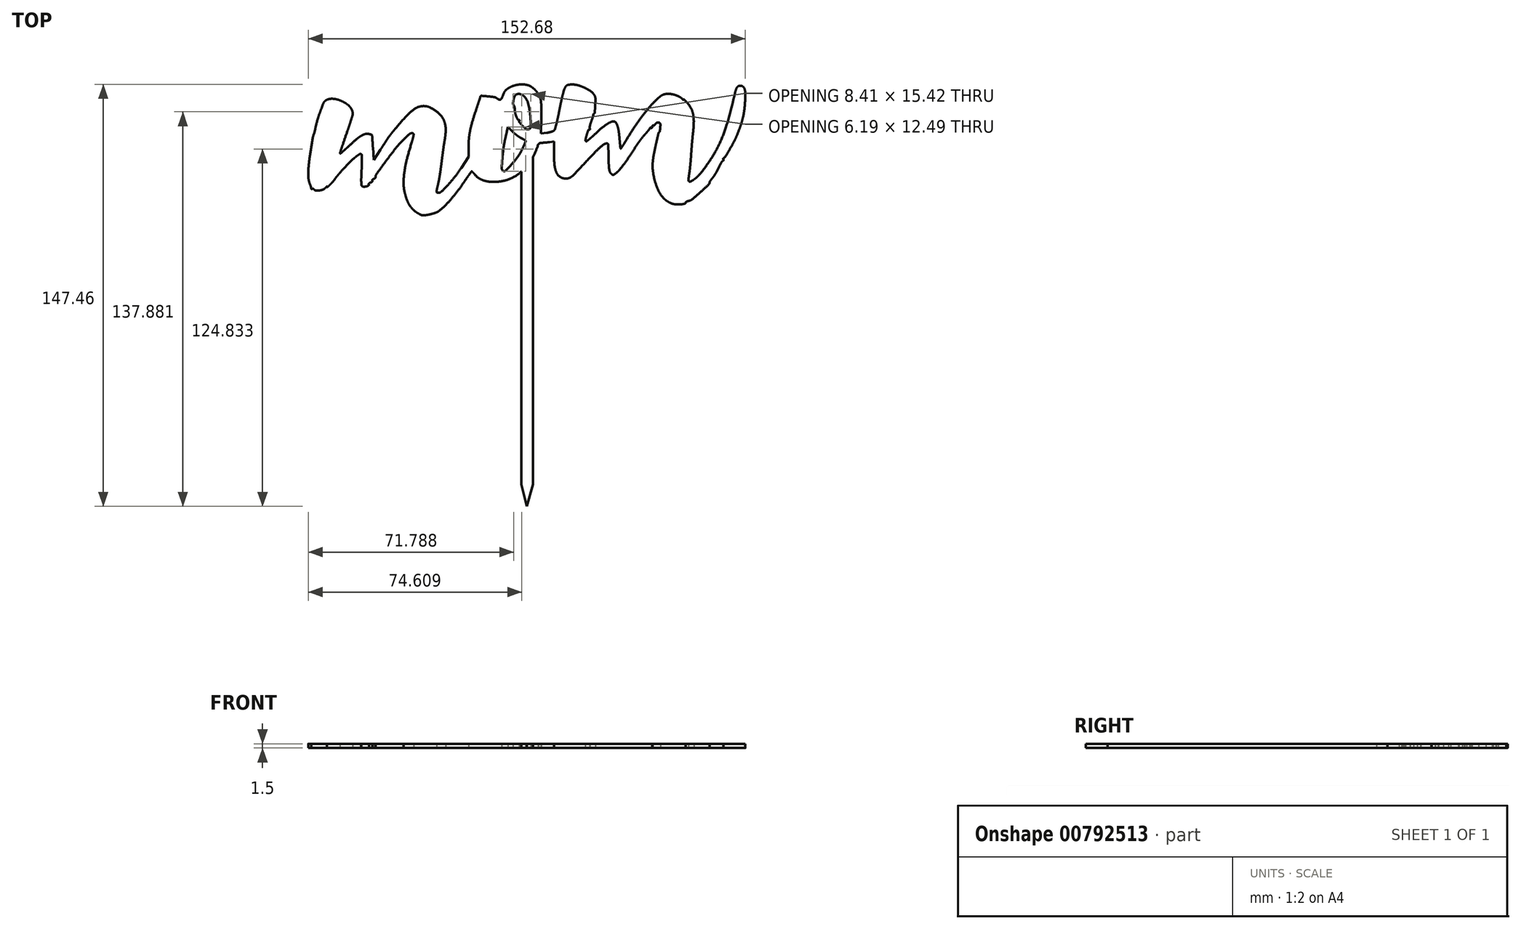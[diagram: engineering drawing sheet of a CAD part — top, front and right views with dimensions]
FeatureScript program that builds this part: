
annotation { "Feature Type Name" : "Feature", "Feature Type Description" : "" }
export const myFeature = defineFeature(function(context is Context, id is Id, definition is map)
    precondition{}
    {
        {
            var Q0;
            Q0=qCreatedBy(makeId("Top.planeOp"),FACE);
            var sketch = newSketch(context, id + "F0", { "sketchPlane" : qUnion([Q0])});
            skArc(sketch, "E0", {"start": v(-5.77, 21.94) * mm, "mid": v(-6.26, 21.68) * mm, "end": v(-6.74, 21.38) * mm});
            skArc(sketch, "E1", {"start": v(-6.74, 21.38) * mm, "mid": v(-7.08, 21.13) * mm, "end": v(-7.4, 20.83) * mm});
            skArc(sketch, "E2", {"start": v(-7.4, 20.83) * mm, "mid": v(-7.65, 20.51) * mm, "end": v(-7.86, 20.17) * mm});
            skArc(sketch, "E3", {"start": v(-7.86, 20.17) * mm, "mid": v(-8.08, 19.71) * mm, "end": v(-8.26, 19.25) * mm});
            skArc(sketch, "E4", {"start": v(-8.26, 19.25) * mm, "mid": v(-8.49, 18.65) * mm, "end": v(-8.74, 18.08) * mm});
            skArc(sketch, "E5", {"start": v(-8.74, 18.08) * mm, "mid": v(-8.93, 17.8) * mm, "end": v(-9.2, 17.62) * mm});
            skArc(sketch, "E6", {"start": v(-9.2, 17.62) * mm, "mid": v(-9.48, 17.55) * mm, "end": v(-9.76, 17.61) * mm});
            skArc(sketch, "E7", {"start": v(-9.76, 17.61) * mm, "mid": v(-10.19, 17.84) * mm, "end": v(-10.59, 18.11) * mm});
            skArc(sketch, "E8", {"start": v(-10.59, 18.11) * mm, "mid": v(-10.99, 18.34) * mm, "end": v(-11.43, 18.46) * mm});
            skArc(sketch, "E9", {"start": v(-11.43, 18.46) * mm, "mid": v(-12.53, 18.61) * mm, "end": v(-13.64, 18.73) * mm});
            skArc(sketch, "E10", {"start": v(-13.64, 18.73) * mm, "mid": v(-14.77, 18.83) * mm, "end": v(-15.91, 18.91) * mm});
            skArc(sketch, "E11", {"start": v(-15.91, 18.91) * mm, "mid": v(-16.11, 18.84) * mm, "end": v(-16.2, 18.65) * mm});
            skArc(sketch, "E12", {"start": v(-16.2, 18.65) * mm, "mid": v(-16.2, 18.6) * mm, "end": v(-16.21, 18.57) * mm});
            skArc(sketch, "E13", {"start": v(-16.21, 18.57) * mm, "mid": v(-16.42, 17.93) * mm, "end": v(-16.63, 17.3) * mm});
            skArc(sketch, "E14", {"start": v(-16.63, 17.3) * mm, "mid": v(-16.87, 16.57) * mm, "end": v(-17.1, 15.86) * mm});
            skArc(sketch, "E15", {"start": v(-17.1, 15.86) * mm, "mid": v(-17.39, 15.02) * mm, "end": v(-17.67, 14.17) * mm});
            skArc(sketch, "E16", {"start": v(-17.67, 14.17) * mm, "mid": v(-18.35, 12.08) * mm, "end": v(-19, 9.97) * mm});
            skArc(sketch, "E17", {"start": v(-19, 9.97) * mm, "mid": v(-19.43, 8.38) * mm, "end": v(-19.8, 6.77) * mm});
            skArc(sketch, "E18", {"start": v(-19.8, 6.77) * mm, "mid": v(-20.05, 5.37) * mm, "end": v(-20.22, 3.97) * mm});
            skArc(sketch, "E19", {"start": v(-20.22, 3.97) * mm, "mid": v(-20.33, 2.51) * mm, "end": v(-20.36, 1.05) * mm});
            skLineSegment(sketch, "E20", {"start": v(-20.36, 1.05) * mm, "end": v(-20.36, -2.42) * mm});
            skLineSegment(sketch, "E21", {"start": v(-20.36, -2.42) * mm, "end": v(-22.92, -6.31) * mm});
            skArc(sketch, "E22", {"start": v(-22.92, -6.31) * mm, "mid": v(-23.98, -7.86) * mm, "end": v(-25.11, -9.37) * mm});
            skArc(sketch, "E23", {"start": v(-25.11, -9.37) * mm, "mid": v(-26.3, -10.83) * mm, "end": v(-27.55, -12.24) * mm});
            skArc(sketch, "E24", {"start": v(-27.55, -12.24) * mm, "mid": v(-28.67, -13.43) * mm, "end": v(-29.83, -14.58) * mm});
            skArc(sketch, "E25", {"start": v(-29.83, -14.58) * mm, "mid": v(-30.34, -14.9) * mm, "end": v(-30.94, -15.02) * mm});
            skArc(sketch, "E26", {"start": v(-30.94, -15.02) * mm, "mid": v(-31.17, -15) * mm, "end": v(-31.38, -14.92) * mm});
            skArc(sketch, "E27", {"start": v(-31.38, -14.92) * mm, "mid": v(-31.5, -14.8) * mm, "end": v(-31.56, -14.65) * mm});
            skArc(sketch, "E28", {"start": v(-31.56, -14.65) * mm, "mid": v(-31.54, -14.33) * mm, "end": v(-31.5, -14.02) * mm});
            skArc(sketch, "E29", {"start": v(-31.5, -14.02) * mm, "mid": v(-31.24, -12.96) * mm, "end": v(-30.99, -11.9) * mm});
            skArc(sketch, "E30", {"start": v(-30.99, -11.9) * mm, "mid": v(-30.84, -11.25) * mm, "end": v(-30.71, -10.59) * mm});
            skArc(sketch, "E31", {"start": v(-30.71, -10.59) * mm, "mid": v(-30.54, -9.6) * mm, "end": v(-30.37, -8.6) * mm});
            skArc(sketch, "E32", {"start": v(-30.37, -8.6) * mm, "mid": v(-30.2, -7.48) * mm, "end": v(-30.04, -6.36) * mm});
            skArc(sketch, "E33", {"start": v(-30.04, -6.36) * mm, "mid": v(-29.9, -5.26) * mm, "end": v(-29.76, -4.17) * mm});
            skArc(sketch, "E34", {"start": v(-29.76, -4.17) * mm, "mid": v(-29.63, -3.09) * mm, "end": v(-29.49, -2) * mm});
            skArc(sketch, "E35", {"start": v(-29.49, -2) * mm, "mid": v(-29.34, -0.92) * mm, "end": v(-29.2, 0.17) * mm});
            skArc(sketch, "E36", {"start": v(-29.2, 0.17) * mm, "mid": v(-29.06, 1.13) * mm, "end": v(-28.92, 2.09) * mm});
            skArc(sketch, "E37", {"start": v(-28.92, 2.09) * mm, "mid": v(-28.82, 2.69) * mm, "end": v(-28.71, 3.29) * mm});
            skArc(sketch, "E38", {"start": v(-28.71, 3.29) * mm, "mid": v(-28.43, 5.29) * mm, "end": v(-28.35, 7.3) * mm});
            skArc(sketch, "E39", {"start": v(-28.35, 7.3) * mm, "mid": v(-28.52, 8.87) * mm, "end": v(-29, 10.38) * mm});
            skArc(sketch, "E40", {"start": v(-29, 10.38) * mm, "mid": v(-29.75, 11.68) * mm, "end": v(-30.75, 12.78) * mm});
            skArc(sketch, "E41", {"start": v(-30.75, 12.78) * mm, "mid": v(-32.16, 13.88) * mm, "end": v(-33.7, 14.77) * mm});
            skArc(sketch, "E42", {"start": v(-33.7, 14.77) * mm, "mid": v(-34.95, 15.21) * mm, "end": v(-36.27, 15.33) * mm});
            skArc(sketch, "E43", {"start": v(-36.27, 15.33) * mm, "mid": v(-37.56, 15.11) * mm, "end": v(-38.76, 14.58) * mm});
            skArc(sketch, "E44", {"start": v(-38.76, 14.58) * mm, "mid": v(-40.32, 13.49) * mm, "end": v(-41.72, 12.2) * mm});
            skArc(sketch, "E45", {"start": v(-41.72, 12.2) * mm, "mid": v(-43.91, 9.78) * mm, "end": v(-46.03, 7.3) * mm});
            skArc(sketch, "E46", {"start": v(-46.03, 7.3) * mm, "mid": v(-46.45, 6.8) * mm, "end": v(-46.85, 6.3) * mm});
            skArc(sketch, "E47", {"start": v(-46.85, 6.3) * mm, "mid": v(-47.24, 5.83) * mm, "end": v(-47.61, 5.35) * mm});
            skArc(sketch, "E48", {"start": v(-47.61, 5.35) * mm, "mid": v(-47.93, 4.94) * mm, "end": v(-48.24, 4.53) * mm});
            skArc(sketch, "E49", {"start": v(-48.24, 4.53) * mm, "mid": v(-48.38, 4.33) * mm, "end": v(-48.51, 4.12) * mm});
            skArc(sketch, "E50", {"start": v(-48.51, 4.12) * mm, "mid": v(-48.65, 3.9) * mm, "end": v(-48.79, 3.68) * mm});
            skArc(sketch, "E51", {"start": v(-48.79, 3.68) * mm, "mid": v(-49.13, 3.15) * mm, "end": v(-49.48, 2.61) * mm});
            skArc(sketch, "E52", {"start": v(-49.48, 2.61) * mm, "mid": v(-49.9, 1.98) * mm, "end": v(-50.31, 1.35) * mm});
            skArc(sketch, "E53", {"start": v(-50.31, 1.35) * mm, "mid": v(-50.77, 0.66) * mm, "end": v(-51.22, -0.02) * mm});
            skLineSegment(sketch, "E54", {"start": v(-51.22, -0.02) * mm, "end": v(-53.52, -3.47) * mm});
            skLineSegment(sketch, "E55", {"start": v(-53.52, -3.47) * mm, "end": v(-53.78, 0.87) * mm});
            skArc(sketch, "E56", {"start": v(-53.78, 0.87) * mm, "mid": v(-53.83, 1.7) * mm, "end": v(-53.88, 2.53) * mm});
            skArc(sketch, "E57", {"start": v(-53.88, 2.53) * mm, "mid": v(-53.93, 3.24) * mm, "end": v(-53.98, 3.94) * mm});
            skArc(sketch, "E58", {"start": v(-53.98, 3.94) * mm, "mid": v(-54.02, 4.57) * mm, "end": v(-54.07, 5.2) * mm});
            skArc(sketch, "E59", {"start": v(-54.07, 5.2) * mm, "mid": v(-54.08, 5.23) * mm, "end": v(-54.1, 5.26) * mm});
            skArc(sketch, "E60", {"start": v(-54.1, 5.26) * mm, "mid": v(-54.11, 5.28) * mm, "end": v(-54.14, 5.29) * mm});
            skArc(sketch, "E61", {"start": v(-54.14, 5.29) * mm, "mid": v(-54.29, 5.33) * mm, "end": v(-54.43, 5.38) * mm});
            skArc(sketch, "E62", {"start": v(-54.43, 5.38) * mm, "mid": v(-54.6, 5.43) * mm, "end": v(-54.78, 5.48) * mm});
            skArc(sketch, "E63", {"start": v(-54.78, 5.48) * mm, "mid": v(-54.99, 5.53) * mm, "end": v(-55.19, 5.58) * mm});
            skArc(sketch, "E64", {"start": v(-55.19, 5.58) * mm, "mid": v(-55.78, 5.65) * mm, "end": v(-56.36, 5.58) * mm});
            skArc(sketch, "E65", {"start": v(-56.36, 5.58) * mm, "mid": v(-57.04, 5.35) * mm, "end": v(-57.68, 5.03) * mm});
            skArc(sketch, "E66", {"start": v(-57.68, 5.03) * mm, "mid": v(-58.55, 4.47) * mm, "end": v(-59.37, 3.83) * mm});
            skArc(sketch, "E67", {"start": v(-59.37, 3.83) * mm, "mid": v(-60.6, 2.76) * mm, "end": v(-61.82, 1.66) * mm});
            skArc(sketch, "E68", {"start": v(-61.82, 1.66) * mm, "mid": v(-62.43, 1.1) * mm, "end": v(-63.04, 0.54) * mm});
            skArc(sketch, "E69", {"start": v(-63.04, 0.54) * mm, "mid": v(-63.57, 0.07) * mm, "end": v(-64.1, -0.4) * mm});
            skArc(sketch, "E70", {"start": v(-64.1, -0.4) * mm, "mid": v(-64.57, -0.81) * mm, "end": v(-65.03, -1.22) * mm});
            skArc(sketch, "E71", {"start": v(-65.03, -1.22) * mm, "mid": v(-65.1, -1.25) * mm, "end": v(-65.16, -1.26) * mm});
            skArc(sketch, "E72", {"start": v(-65.16, -1.26) * mm, "mid": v(-65.25, -1.22) * mm, "end": v(-65.26, -1.12) * mm});
            skArc(sketch, "E73", {"start": v(-65.26, -1.12) * mm, "mid": v(-65.1, -0.56) * mm, "end": v(-64.93, 0) * mm});
            skArc(sketch, "E74", {"start": v(-64.93, 0) * mm, "mid": v(-64.62, 0.96) * mm, "end": v(-64.3, 1.91) * mm});
            skArc(sketch, "E75", {"start": v(-64.3, 1.91) * mm, "mid": v(-63.51, 4.18) * mm, "end": v(-62.72, 6.45) * mm});
            skArc(sketch, "E76", {"start": v(-62.72, 6.45) * mm, "mid": v(-62.36, 7.52) * mm, "end": v(-62, 8.58) * mm});
            skArc(sketch, "E77", {"start": v(-62, 8.58) * mm, "mid": v(-61.69, 9.54) * mm, "end": v(-61.39, 10.5) * mm});
            skArc(sketch, "E78", {"start": v(-61.39, 10.5) * mm, "mid": v(-61.14, 11.3) * mm, "end": v(-60.9, 12.12) * mm});
            skArc(sketch, "E79", {"start": v(-60.9, 12.12) * mm, "mid": v(-60.85, 12.37) * mm, "end": v(-60.83, 12.62) * mm});
            skArc(sketch, "E80", {"start": v(-60.83, 12.62) * mm, "mid": v(-60.88, 13.21) * mm, "end": v(-61.04, 13.78) * mm});
            skArc(sketch, "E81", {"start": v(-61.04, 13.78) * mm, "mid": v(-61.33, 14.37) * mm, "end": v(-61.7, 14.91) * mm});
            skArc(sketch, "E82", {"start": v(-61.7, 14.91) * mm, "mid": v(-62.21, 15.47) * mm, "end": v(-62.79, 15.95) * mm});
            skArc(sketch, "E83", {"start": v(-62.79, 15.95) * mm, "mid": v(-63.48, 16.42) * mm, "end": v(-64.22, 16.83) * mm});
            skArc(sketch, "E84", {"start": v(-64.22, 16.83) * mm, "mid": v(-65.13, 17.24) * mm, "end": v(-66.06, 17.57) * mm});
            skArc(sketch, "E85", {"start": v(-66.06, 17.57) * mm, "mid": v(-66.9, 17.77) * mm, "end": v(-67.77, 17.87) * mm});
            skArc(sketch, "E86", {"start": v(-67.77, 17.87) * mm, "mid": v(-68.52, 17.86) * mm, "end": v(-69.25, 17.74) * mm});
            skArc(sketch, "E87", {"start": v(-69.25, 17.74) * mm, "mid": v(-69.85, 17.52) * mm, "end": v(-70.4, 17.18) * mm});
            skArc(sketch, "E88", {"start": v(-70.4, 17.18) * mm, "mid": v(-70.8, 16.74) * mm, "end": v(-71.1, 16.22) * mm});
            skArc(sketch, "E89", {"start": v(-71.1, 16.22) * mm, "mid": v(-71.68, 14.73) * mm, "end": v(-72.23, 13.23) * mm});
            skArc(sketch, "E90", {"start": v(-72.23, 13.23) * mm, "mid": v(-72.78, 11.6) * mm, "end": v(-73.28, 9.96) * mm});
            skArc(sketch, "E91", {"start": v(-73.28, 9.96) * mm, "mid": v(-73.66, 8.53) * mm, "end": v(-73.98, 7.08) * mm});
            skArc(sketch, "E92", {"start": v(-73.98, 7.08) * mm, "mid": v(-74.03, 6.85) * mm, "end": v(-74.08, 6.63) * mm});
            skArc(sketch, "E93", {"start": v(-74.08, 6.63) * mm, "mid": v(-74.14, 6.4) * mm, "end": v(-74.2, 6.16) * mm});
            skArc(sketch, "E94", {"start": v(-74.2, 6.16) * mm, "mid": v(-74.26, 5.94) * mm, "end": v(-74.33, 5.72) * mm});
            skArc(sketch, "E95", {"start": v(-74.33, 5.72) * mm, "mid": v(-74.38, 5.56) * mm, "end": v(-74.44, 5.4) * mm});
            skArc(sketch, "E96", {"start": v(-74.44, 5.4) * mm, "mid": v(-74.5, 5.26) * mm, "end": v(-74.55, 5.1) * mm});
            skArc(sketch, "E97", {"start": v(-74.55, 5.1) * mm, "mid": v(-74.61, 4.92) * mm, "end": v(-74.67, 4.72) * mm});
            skArc(sketch, "E98", {"start": v(-74.67, 4.72) * mm, "mid": v(-74.72, 4.52) * mm, "end": v(-74.77, 4.31) * mm});
            skArc(sketch, "E99", {"start": v(-74.77, 4.31) * mm, "mid": v(-74.8, 4.13) * mm, "end": v(-74.84, 3.95) * mm});
            skArc(sketch, "E100", {"start": v(-74.84, 3.95) * mm, "mid": v(-75.37, 0.74) * mm, "end": v(-75.86, -2.48) * mm});
            skArc(sketch, "E101", {"start": v(-75.86, -2.48) * mm, "mid": v(-76.12, -4.63) * mm, "end": v(-76.3, -6.78) * mm});
            skArc(sketch, "E102", {"start": v(-76.3, -6.78) * mm, "mid": v(-76.34, -8.3) * mm, "end": v(-76.3, -9.8) * mm});
            skArc(sketch, "E103", {"start": v(-76.3, -9.8) * mm, "mid": v(-76.13, -10.87) * mm, "end": v(-75.8, -11.9) * mm});
            skArc(sketch, "E104", {"start": v(-75.8, -11.9) * mm, "mid": v(-75.7, -12.15) * mm, "end": v(-75.6, -12.4) * mm});
            skArc(sketch, "E105", {"start": v(-75.6, -12.4) * mm, "mid": v(-75.52, -12.64) * mm, "end": v(-75.45, -12.88) * mm});
            skArc(sketch, "E106", {"start": v(-75.45, -12.88) * mm, "mid": v(-75.4, -13.08) * mm, "end": v(-75.35, -13.29) * mm});
            skArc(sketch, "E107", {"start": v(-75.35, -13.29) * mm, "mid": v(-75.34, -13.4) * mm, "end": v(-75.35, -13.5) * mm});
            skArc(sketch, "E108", {"start": v(-75.35, -13.5) * mm, "mid": v(-75.36, -13.55) * mm, "end": v(-75.35, -13.6) * mm});
            skArc(sketch, "E109", {"start": v(-75.35, -13.6) * mm, "mid": v(-75.33, -13.64) * mm, "end": v(-75.3, -13.66) * mm});
            skArc(sketch, "E110", {"start": v(-75.3, -13.66) * mm, "mid": v(-75.23, -13.67) * mm, "end": v(-75.18, -13.66) * mm});
            skArc(sketch, "E111", {"start": v(-75.18, -13.66) * mm, "mid": v(-75.1, -13.63) * mm, "end": v(-75.03, -13.59) * mm});
            skArc(sketch, "E112", {"start": v(-75.03, -13.59) * mm, "mid": v(-74.95, -13.55) * mm, "end": v(-74.86, -13.53) * mm});
            skArc(sketch, "E113", {"start": v(-74.86, -13.53) * mm, "mid": v(-74.77, -13.52) * mm, "end": v(-74.67, -13.54) * mm});
            skArc(sketch, "E114", {"start": v(-74.67, -13.54) * mm, "mid": v(-74.58, -13.57) * mm, "end": v(-74.5, -13.62) * mm});
            skArc(sketch, "E115", {"start": v(-74.5, -13.62) * mm, "mid": v(-74.43, -13.69) * mm, "end": v(-74.37, -13.77) * mm});
            skArc(sketch, "E116", {"start": v(-74.37, -13.77) * mm, "mid": v(-74.1, -14.05) * mm, "end": v(-73.72, -14.19) * mm});
            skArc(sketch, "E117", {"start": v(-73.72, -14.19) * mm, "mid": v(-73.1, -14.23) * mm, "end": v(-72.5, -14.19) * mm});
            skArc(sketch, "E118", {"start": v(-72.5, -14.19) * mm, "mid": v(-71.84, -14.06) * mm, "end": v(-71.2, -13.86) * mm});
            skArc(sketch, "E119", {"start": v(-71.2, -13.86) * mm, "mid": v(-70.73, -13.6) * mm, "end": v(-70.34, -13.25) * mm});
            skArc(sketch, "E120", {"start": v(-70.34, -13.25) * mm, "mid": v(-70.19, -13.09) * mm, "end": v(-70.03, -12.92) * mm});
            skArc(sketch, "E121", {"start": v(-70.03, -12.92) * mm, "mid": v(-69.94, -12.84) * mm, "end": v(-69.85, -12.77) * mm});
            skArc(sketch, "E122", {"start": v(-69.85, -12.77) * mm, "mid": v(-69.81, -12.77) * mm, "end": v(-69.8, -12.8) * mm});
            skArc(sketch, "E123", {"start": v(-69.8, -12.8) * mm, "mid": v(-69.8, -12.87) * mm, "end": v(-69.83, -12.94) * mm});
            skArc(sketch, "E124", {"start": v(-69.83, -12.94) * mm, "mid": v(-69.82, -12.99) * mm, "end": v(-69.78, -13) * mm});
            skArc(sketch, "E125", {"start": v(-69.78, -13) * mm, "mid": v(-69.7, -12.98) * mm, "end": v(-69.62, -12.93) * mm});
            skArc(sketch, "E126", {"start": v(-69.62, -12.93) * mm, "mid": v(-69.4, -12.77) * mm, "end": v(-69.21, -12.59) * mm});
            skArc(sketch, "E127", {"start": v(-69.21, -12.59) * mm, "mid": v(-68.93, -12.32) * mm, "end": v(-68.66, -12.04) * mm});
            skArc(sketch, "E128", {"start": v(-68.66, -12.04) * mm, "mid": v(-68.36, -11.74) * mm, "end": v(-68.08, -11.43) * mm});
            skArc(sketch, "E129", {"start": v(-68.08, -11.43) * mm, "mid": v(-67.82, -11.14) * mm, "end": v(-67.56, -10.85) * mm});
            skArc(sketch, "E130", {"start": v(-67.56, -10.85) * mm, "mid": v(-67.35, -10.6) * mm, "end": v(-67.15, -10.35) * mm});
            skArc(sketch, "E131", {"start": v(-67.15, -10.35) * mm, "mid": v(-67.07, -10.24) * mm, "end": v(-67.01, -10.12) * mm});
            skArc(sketch, "E132", {"start": v(-67.01, -10.12) * mm, "mid": v(-66.95, -9.98) * mm, "end": v(-66.86, -9.86) * mm});
            skArc(sketch, "E133", {"start": v(-66.86, -9.86) * mm, "mid": v(-66.46, -9.37) * mm, "end": v(-66.05, -8.88) * mm});
            skArc(sketch, "E134", {"start": v(-66.05, -8.88) * mm, "mid": v(-65.56, -8.31) * mm, "end": v(-65.07, -7.75) * mm});
            skArc(sketch, "E135", {"start": v(-65.07, -7.75) * mm, "mid": v(-64.5, -7.11) * mm, "end": v(-63.94, -6.48) * mm});
            skArc(sketch, "E136", {"start": v(-63.94, -6.48) * mm, "mid": v(-62.9, -5.35) * mm, "end": v(-61.82, -4.25) * mm});
            skArc(sketch, "E137", {"start": v(-61.82, -4.25) * mm, "mid": v(-60.93, -3.4) * mm, "end": v(-59.99, -2.6) * mm});
            skArc(sketch, "E138", {"start": v(-59.99, -2.6) * mm, "mid": v(-59.26, -2.05) * mm, "end": v(-58.5, -1.53) * mm});
            skArc(sketch, "E139", {"start": v(-58.5, -1.53) * mm, "mid": v(-58.16, -1.43) * mm, "end": v(-57.81, -1.52) * mm});
            skArc(sketch, "E140", {"start": v(-57.81, -1.52) * mm, "mid": v(-57.71, -1.62) * mm, "end": v(-57.67, -1.76) * mm});
            skArc(sketch, "E141", {"start": v(-57.67, -1.76) * mm, "mid": v(-57.65, -2.5) * mm, "end": v(-57.64, -3.25) * mm});
            skArc(sketch, "E142", {"start": v(-57.64, -3.25) * mm, "mid": v(-57.64, -4.13) * mm, "end": v(-57.65, -5.02) * mm});
            skArc(sketch, "E143", {"start": v(-57.65, -5.02) * mm, "mid": v(-57.68, -6.04) * mm, "end": v(-57.73, -7.07) * mm});
            skArc(sketch, "E144", {"start": v(-57.73, -7.07) * mm, "mid": v(-57.8, -8.37) * mm, "end": v(-57.84, -9.66) * mm});
            skArc(sketch, "E145", {"start": v(-57.84, -9.66) * mm, "mid": v(-57.86, -10.48) * mm, "end": v(-57.84, -11.29) * mm});
            skArc(sketch, "E146", {"start": v(-57.84, -11.29) * mm, "mid": v(-57.8, -11.82) * mm, "end": v(-57.75, -12.34) * mm});
            skArc(sketch, "E147", {"start": v(-57.75, -12.34) * mm, "mid": v(-57.67, -12.55) * mm, "end": v(-57.51, -12.7) * mm});
            skArc(sketch, "E148", {"start": v(-57.51, -12.7) * mm, "mid": v(-57.2, -12.84) * mm, "end": v(-56.87, -12.88) * mm});
            skArc(sketch, "E149", {"start": v(-56.87, -12.88) * mm, "mid": v(-56.42, -12.84) * mm, "end": v(-55.98, -12.75) * mm});
            skArc(sketch, "E150", {"start": v(-55.98, -12.75) * mm, "mid": v(-55.62, -12.62) * mm, "end": v(-55.3, -12.43) * mm});
            skArc(sketch, "E151", {"start": v(-55.3, -12.43) * mm, "mid": v(-55.18, -12.27) * mm, "end": v(-55.2, -12.07) * mm});
            skArc(sketch, "E152", {"start": v(-55.2, -12.07) * mm, "mid": v(-55.24, -11.98) * mm, "end": v(-55.24, -11.88) * mm});
            skArc(sketch, "E153", {"start": v(-55.24, -11.88) * mm, "mid": v(-55.2, -11.78) * mm, "end": v(-55.14, -11.7) * mm});
            skArc(sketch, "E154", {"start": v(-55.14, -11.7) * mm, "mid": v(-55.04, -11.6) * mm, "end": v(-54.92, -11.52) * mm});
            skArc(sketch, "E155", {"start": v(-54.92, -11.52) * mm, "mid": v(-54.77, -11.46) * mm, "end": v(-54.6, -11.4) * mm});
            skArc(sketch, "E156", {"start": v(-54.6, -11.4) * mm, "mid": v(-54.44, -11.35) * mm, "end": v(-54.29, -11.3) * mm});
            skArc(sketch, "E157", {"start": v(-54.29, -11.3) * mm, "mid": v(-54.17, -11.22) * mm, "end": v(-54.06, -11.13) * mm});
            skArc(sketch, "E158", {"start": v(-54.06, -11.13) * mm, "mid": v(-54, -11.06) * mm, "end": v(-53.95, -10.96) * mm});
            skArc(sketch, "E159", {"start": v(-53.95, -10.96) * mm, "mid": v(-53.94, -10.88) * mm, "end": v(-53.96, -10.8) * mm});
            skArc(sketch, "E160", {"start": v(-53.96, -10.8) * mm, "mid": v(-54, -10.73) * mm, "end": v(-54, -10.64) * mm});
            skArc(sketch, "E161", {"start": v(-54, -10.64) * mm, "mid": v(-53.98, -10.55) * mm, "end": v(-53.94, -10.47) * mm});
            skArc(sketch, "E162", {"start": v(-53.94, -10.47) * mm, "mid": v(-53.86, -10.38) * mm, "end": v(-53.78, -10.3) * mm});
            skArc(sketch, "E163", {"start": v(-53.78, -10.3) * mm, "mid": v(-53.66, -10.24) * mm, "end": v(-53.54, -10.18) * mm});
            skArc(sketch, "E164", {"start": v(-53.54, -10.18) * mm, "mid": v(-53.42, -10.13) * mm, "end": v(-53.3, -10.06) * mm});
            skArc(sketch, "E165", {"start": v(-53.3, -10.06) * mm, "mid": v(-53.18, -9.98) * mm, "end": v(-53.08, -9.9) * mm});
            skArc(sketch, "E166", {"start": v(-53.08, -9.9) * mm, "mid": v(-53, -9.8) * mm, "end": v(-52.94, -9.72) * mm});
            skArc(sketch, "E167", {"start": v(-52.94, -9.72) * mm, "mid": v(-52.9, -9.64) * mm, "end": v(-52.9, -9.55) * mm});
            skArc(sketch, "E168", {"start": v(-52.9, -9.55) * mm, "mid": v(-52.8, -9) * mm, "end": v(-52.56, -8.51) * mm});
            skArc(sketch, "E169", {"start": v(-52.56, -8.51) * mm, "mid": v(-50.9, -6.22) * mm, "end": v(-49.24, -3.94) * mm});
            skArc(sketch, "E170", {"start": v(-49.24, -3.94) * mm, "mid": v(-47.62, -1.77) * mm, "end": v(-45.97, 0.37) * mm});
            skArc(sketch, "E171", {"start": v(-45.97, 0.37) * mm, "mid": v(-44.85, 1.71) * mm, "end": v(-43.67, 3) * mm});
            skArc(sketch, "E172", {"start": v(-43.67, 3) * mm, "mid": v(-42.43, 4.23) * mm, "end": v(-41.16, 5.43) * mm});
            skArc(sketch, "E173", {"start": v(-41.16, 5.43) * mm, "mid": v(-40.63, 5.75) * mm, "end": v(-40.03, 5.85) * mm});
            skArc(sketch, "E174", {"start": v(-40.03, 5.85) * mm, "mid": v(-39.65, 5.66) * mm, "end": v(-39.54, 5.25) * mm});
            skArc(sketch, "E175", {"start": v(-39.54, 5.25) * mm, "mid": v(-39.8, 4.05) * mm, "end": v(-40.14, 2.88) * mm});
            skArc(sketch, "E176", {"start": v(-40.14, 2.88) * mm, "mid": v(-41.03, -0.05) * mm, "end": v(-41.83, -3) * mm});
            skArc(sketch, "E177", {"start": v(-41.83, -3) * mm, "mid": v(-42.37, -5.34) * mm, "end": v(-42.78, -7.7) * mm});
            skArc(sketch, "E178", {"start": v(-42.78, -7.7) * mm, "mid": v(-42.99, -9.64) * mm, "end": v(-43.05, -11.58) * mm});
            skArc(sketch, "E179", {"start": v(-43.05, -11.58) * mm, "mid": v(-42.96, -13.24) * mm, "end": v(-42.67, -14.88) * mm});
            skArc(sketch, "E180", {"start": v(-42.67, -14.88) * mm, "mid": v(-42.35, -16.11) * mm, "end": v(-41.96, -17.32) * mm});
            skArc(sketch, "E181", {"start": v(-41.96, -17.32) * mm, "mid": v(-41.55, -18.3) * mm, "end": v(-41.04, -19.22) * mm});
            skArc(sketch, "E182", {"start": v(-41.04, -19.22) * mm, "mid": v(-40.5, -20) * mm, "end": v(-39.87, -20.72) * mm});
            skArc(sketch, "E183", {"start": v(-39.87, -20.72) * mm, "mid": v(-39.15, -21.36) * mm, "end": v(-38.37, -21.92) * mm});
            skArc(sketch, "E184", {"start": v(-38.37, -21.92) * mm, "mid": v(-37.78, -22.28) * mm, "end": v(-37.18, -22.62) * mm});
            skArc(sketch, "E185", {"start": v(-37.18, -22.62) * mm, "mid": v(-36.82, -22.77) * mm, "end": v(-36.44, -22.86) * mm});
            skArc(sketch, "E186", {"start": v(-36.44, -22.86) * mm, "mid": v(-36.03, -22.9) * mm, "end": v(-35.61, -22.86) * mm});
            skArc(sketch, "E187", {"start": v(-35.61, -22.86) * mm, "mid": v(-34.83, -22.73) * mm, "end": v(-34.05, -22.58) * mm});
            skArc(sketch, "E188", {"start": v(-34.05, -22.58) * mm, "mid": v(-33.55, -22.47) * mm, "end": v(-33.04, -22.34) * mm});
            skArc(sketch, "E189", {"start": v(-33.04, -22.34) * mm, "mid": v(-32.54, -22.18) * mm, "end": v(-32.04, -22.01) * mm});
            skArc(sketch, "E190", {"start": v(-32.04, -22.01) * mm, "mid": v(-31.6, -21.85) * mm, "end": v(-31.18, -21.67) * mm});
            skArc(sketch, "E191", {"start": v(-31.18, -21.67) * mm, "mid": v(-30.92, -21.53) * mm, "end": v(-30.67, -21.36) * mm});
            skArc(sketch, "E192", {"start": v(-30.67, -21.36) * mm, "mid": v(-29.68, -20.55) * mm, "end": v(-28.75, -19.67) * mm});
            skArc(sketch, "E193", {"start": v(-28.75, -19.67) * mm, "mid": v(-27.63, -18.52) * mm, "end": v(-26.56, -17.33) * mm});
            skArc(sketch, "E194", {"start": v(-26.56, -17.33) * mm, "mid": v(-25.43, -16) * mm, "end": v(-24.34, -14.62) * mm});
            skArc(sketch, "E195", {"start": v(-24.34, -14.62) * mm, "mid": v(-23.3, -13.22) * mm, "end": v(-22.3, -11.78) * mm});
            skArc(sketch, "E196", {"start": v(-22.3, -11.78) * mm, "mid": v(-21.75, -10.96) * mm, "end": v(-21.19, -10.15) * mm});
            skArc(sketch, "E197", {"start": v(-21.19, -10.15) * mm, "mid": v(-20.7, -9.46) * mm, "end": v(-20.22, -8.77) * mm});
            skArc(sketch, "E198", {"start": v(-20.22, -8.77) * mm, "mid": v(-19.79, -8.18) * mm, "end": v(-19.36, -7.58) * mm});
            skArc(sketch, "E199", {"start": v(-19.36, -7.58) * mm, "mid": v(-19.3, -7.54) * mm, "end": v(-19.23, -7.52) * mm});
            skArc(sketch, "E200", {"start": v(-19.23, -7.52) * mm, "mid": v(-19.17, -7.53) * mm, "end": v(-19.11, -7.56) * mm});
            skArc(sketch, "E201", {"start": v(-19.11, -7.56) * mm, "mid": v(-18.98, -7.7) * mm, "end": v(-18.84, -7.83) * mm});
            skArc(sketch, "E202", {"start": v(-18.84, -7.83) * mm, "mid": v(-18.68, -8) * mm, "end": v(-18.53, -8.17) * mm});
            skArc(sketch, "E203", {"start": v(-18.53, -8.17) * mm, "mid": v(-18.36, -8.37) * mm, "end": v(-18.2, -8.57) * mm});
            skArc(sketch, "E204", {"start": v(-18.2, -8.57) * mm, "mid": v(-17.35, -9.44) * mm, "end": v(-16.35, -10.12) * mm});
            skArc(sketch, "E205", {"start": v(-16.35, -10.12) * mm, "mid": v(-15.12, -10.66) * mm, "end": v(-13.82, -11) * mm});
            skArc(sketch, "E206", {"start": v(-13.82, -11) * mm, "mid": v(-12.29, -11.2) * mm, "end": v(-10.74, -11.17) * mm});
            skArc(sketch, "E207", {"start": v(-10.74, -11.17) * mm, "mid": v(-9, -10.96) * mm, "end": v(-7.29, -10.6) * mm});
            skArc(sketch, "E208", {"start": v(-7.29, -10.6) * mm, "mid": v(-5.5, -9.97) * mm, "end": v(-3.86, -9.06) * mm});
            skArc(sketch, "E209", {"start": v(-3.86, -9.06) * mm, "mid": v(-2.18, -7.78) * mm, "end": v(-0.67, -6.31) * mm});
            skArc(sketch, "E210", {"start": v(-0.67, -6.31) * mm, "mid": v(0.78, -4.53) * mm, "end": v(2.02, -2.6) * mm});
            skArc(sketch, "E211", {"start": v(2.02, -2.6) * mm, "mid": v(3.1, -0.47) * mm, "end": v(3.97, 1.76) * mm});
            skArc(sketch, "E212", {"start": v(3.97, 1.76) * mm, "mid": v(4.04, 1.92) * mm, "end": v(4.15, 2.07) * mm});
            skArc(sketch, "E213", {"start": v(4.15, 2.07) * mm, "mid": v(4.3, 2.2) * mm, "end": v(4.45, 2.3) * mm});
            skArc(sketch, "E214", {"start": v(4.45, 2.3) * mm, "mid": v(4.66, 2.39) * mm, "end": v(4.87, 2.44) * mm});
            skArc(sketch, "E215", {"start": v(4.87, 2.44) * mm, "mid": v(5.12, 2.48) * mm, "end": v(5.37, 2.5) * mm});
            skArc(sketch, "E216", {"start": v(5.37, 2.5) * mm, "mid": v(5.65, 2.5) * mm, "end": v(5.92, 2.51) * mm});
            skArc(sketch, "E217", {"start": v(5.92, 2.51) * mm, "mid": v(6.28, 2.54) * mm, "end": v(6.63, 2.57) * mm});
            skArc(sketch, "E218", {"start": v(6.63, 2.57) * mm, "mid": v(7, 2.6) * mm, "end": v(7.37, 2.65) * mm});
            skArc(sketch, "E219", {"start": v(7.37, 2.65) * mm, "mid": v(7.7, 2.7) * mm, "end": v(8.02, 2.75) * mm});
            skLineSegment(sketch, "E220", {"start": v(8.02, 2.75) * mm, "end": v(9.51, 3) * mm});
            skLineSegment(sketch, "E221", {"start": v(9.51, 3) * mm, "end": v(9.49, -1.12) * mm});
            skArc(sketch, "E222", {"start": v(9.49, -1.12) * mm, "mid": v(9.53, -3.2) * mm, "end": v(9.68, -5.3) * mm});
            skArc(sketch, "E223", {"start": v(9.68, -5.3) * mm, "mid": v(9.93, -6.66) * mm, "end": v(10.4, -7.97) * mm});
            skArc(sketch, "E224", {"start": v(10.4, -7.97) * mm, "mid": v(10.94, -8.8) * mm, "end": v(11.68, -9.46) * mm});
            skArc(sketch, "E225", {"start": v(11.68, -9.46) * mm, "mid": v(12.58, -9.88) * mm, "end": v(13.55, -10.02) * mm});
            skArc(sketch, "E226", {"start": v(13.55, -10.02) * mm, "mid": v(14.1, -9.99) * mm, "end": v(14.62, -9.88) * mm});
            skArc(sketch, "E227", {"start": v(14.62, -9.88) * mm, "mid": v(15.07, -9.72) * mm, "end": v(15.48, -9.48) * mm});
            skArc(sketch, "E228", {"start": v(15.48, -9.48) * mm, "mid": v(16.02, -9.06) * mm, "end": v(16.51, -8.59) * mm});
            skArc(sketch, "E229", {"start": v(16.51, -8.59) * mm, "mid": v(17.56, -7.5) * mm, "end": v(18.6, -6.39) * mm});
            skArc(sketch, "E230", {"start": v(18.6, -6.39) * mm, "mid": v(21.18, -3.62) * mm, "end": v(23.78, -0.88) * mm});
            skArc(sketch, "E231", {"start": v(23.78, -0.88) * mm, "mid": v(25.08, 0.4) * mm, "end": v(26.45, 1.6) * mm});
            skArc(sketch, "E232", {"start": v(26.45, 1.6) * mm, "mid": v(27.1, 2.01) * mm, "end": v(27.81, 2.26) * mm});
            skArc(sketch, "E233", {"start": v(27.81, 2.26) * mm, "mid": v(28.25, 2.16) * mm, "end": v(28.46, 1.76) * mm});
            skArc(sketch, "E234", {"start": v(28.46, 1.76) * mm, "mid": v(28.47, 1.52) * mm, "end": v(28.48, 1.28) * mm});
            skArc(sketch, "E235", {"start": v(28.48, 1.28) * mm, "mid": v(28.5, 0.63) * mm, "end": v(28.51, -0.01) * mm});
            skArc(sketch, "E236", {"start": v(28.51, -0.01) * mm, "mid": v(28.53, -0.79) * mm, "end": v(28.55, -1.56) * mm});
            skArc(sketch, "E237", {"start": v(28.55, -1.56) * mm, "mid": v(28.57, -2.4) * mm, "end": v(28.59, -3.25) * mm});
            skArc(sketch, "E238", {"start": v(28.59, -3.25) * mm, "mid": v(28.62, -4.36) * mm, "end": v(28.66, -5.46) * mm});
            skArc(sketch, "E239", {"start": v(28.66, -5.46) * mm, "mid": v(28.71, -6.13) * mm, "end": v(28.8, -6.8) * mm});
            skArc(sketch, "E240", {"start": v(28.8, -6.8) * mm, "mid": v(28.9, -7.24) * mm, "end": v(29.03, -7.68) * mm});
            skArc(sketch, "E241", {"start": v(29.03, -7.68) * mm, "mid": v(29.17, -7.98) * mm, "end": v(29.38, -8.24) * mm});
            skArc(sketch, "E242", {"start": v(29.38, -8.24) * mm, "mid": v(29.6, -8.44) * mm, "end": v(29.83, -8.62) * mm});
            skArc(sketch, "E243", {"start": v(29.83, -8.62) * mm, "mid": v(29.98, -8.7) * mm, "end": v(30.15, -8.7) * mm});
            skArc(sketch, "E244", {"start": v(30.15, -8.7) * mm, "mid": v(30.34, -8.67) * mm, "end": v(30.52, -8.58) * mm});
            skArc(sketch, "E245", {"start": v(30.52, -8.58) * mm, "mid": v(30.88, -8.34) * mm, "end": v(31.24, -8.08) * mm});
            skArc(sketch, "E246", {"start": v(31.24, -8.08) * mm, "mid": v(31.82, -7.59) * mm, "end": v(32.35, -7.02) * mm});
            skArc(sketch, "E247", {"start": v(32.35, -7.02) * mm, "mid": v(33.25, -5.89) * mm, "end": v(34.12, -4.73) * mm});
            skArc(sketch, "E248", {"start": v(34.12, -4.73) * mm, "mid": v(35.12, -3.35) * mm, "end": v(36.1, -1.95) * mm});
            skArc(sketch, "E249", {"start": v(36.1, -1.95) * mm, "mid": v(37.07, -0.46) * mm, "end": v(38.02, 1.05) * mm});
            skArc(sketch, "E250", {"start": v(38.02, 1.05) * mm, "mid": v(38.35, 1.58) * mm, "end": v(38.7, 2.1) * mm});
            skArc(sketch, "E251", {"start": v(38.7, 2.1) * mm, "mid": v(39.13, 2.7) * mm, "end": v(39.57, 3.3) * mm});
            skArc(sketch, "E252", {"start": v(39.57, 3.3) * mm, "mid": v(40, 3.88) * mm, "end": v(40.46, 4.45) * mm});
            skArc(sketch, "E253", {"start": v(40.46, 4.45) * mm, "mid": v(40.84, 4.9) * mm, "end": v(41.24, 5.36) * mm});
            skArc(sketch, "E254", {"start": v(41.24, 5.36) * mm, "mid": v(41.59, 5.74) * mm, "end": v(41.92, 6.12) * mm});
            skArc(sketch, "E255", {"start": v(41.92, 6.12) * mm, "mid": v(42.21, 6.47) * mm, "end": v(42.5, 6.82) * mm});
            skArc(sketch, "E256", {"start": v(42.5, 6.82) * mm, "mid": v(42.72, 7.11) * mm, "end": v(42.95, 7.41) * mm});
            skArc(sketch, "E257", {"start": v(42.95, 7.41) * mm, "mid": v(43, 7.51) * mm, "end": v(43.02, 7.62) * mm});
            skArc(sketch, "E258", {"start": v(43.02, 7.62) * mm, "mid": v(43.03, 7.68) * mm, "end": v(43.05, 7.73) * mm});
            skArc(sketch, "E259", {"start": v(43.05, 7.73) * mm, "mid": v(43.1, 7.77) * mm, "end": v(43.14, 7.78) * mm});
            skArc(sketch, "E260", {"start": v(43.14, 7.78) * mm, "mid": v(43.2, 7.79) * mm, "end": v(43.28, 7.78) * mm});
            skArc(sketch, "E261", {"start": v(43.28, 7.78) * mm, "mid": v(43.36, 7.74) * mm, "end": v(43.44, 7.7) * mm});
            skArc(sketch, "E262", {"start": v(43.44, 7.7) * mm, "mid": v(43.51, 7.67) * mm, "end": v(43.6, 7.66) * mm});
            skArc(sketch, "E263", {"start": v(43.6, 7.66) * mm, "mid": v(43.67, 7.68) * mm, "end": v(43.73, 7.72) * mm});
            skArc(sketch, "E264", {"start": v(43.73, 7.72) * mm, "mid": v(43.79, 7.8) * mm, "end": v(43.82, 7.88) * mm});
            skArc(sketch, "E265", {"start": v(43.82, 7.88) * mm, "mid": v(43.85, 8) * mm, "end": v(43.85, 8.12) * mm});
            skArc(sketch, "E266", {"start": v(43.85, 8.12) * mm, "mid": v(43.86, 8.24) * mm, "end": v(43.88, 8.36) * mm});
            skArc(sketch, "E267", {"start": v(43.88, 8.36) * mm, "mid": v(43.91, 8.45) * mm, "end": v(43.96, 8.53) * mm});
            skArc(sketch, "E268", {"start": v(43.96, 8.53) * mm, "mid": v(44.02, 8.57) * mm, "end": v(44.09, 8.6) * mm});
            skArc(sketch, "E269", {"start": v(44.09, 8.6) * mm, "mid": v(44.16, 8.6) * mm, "end": v(44.23, 8.56) * mm});
            skArc(sketch, "E270", {"start": v(44.23, 8.56) * mm, "mid": v(44.3, 8.53) * mm, "end": v(44.39, 8.52) * mm});
            skArc(sketch, "E271", {"start": v(44.39, 8.52) * mm, "mid": v(44.48, 8.54) * mm, "end": v(44.56, 8.58) * mm});
            skArc(sketch, "E272", {"start": v(44.56, 8.58) * mm, "mid": v(44.65, 8.65) * mm, "end": v(44.72, 8.73) * mm});
            skArc(sketch, "E273", {"start": v(44.72, 8.73) * mm, "mid": v(44.79, 8.84) * mm, "end": v(44.84, 8.96) * mm});
            skArc(sketch, "E274", {"start": v(44.84, 8.96) * mm, "mid": v(44.9, 9.08) * mm, "end": v(45, 9.2) * mm});
            skArc(sketch, "E275", {"start": v(45, 9.2) * mm, "mid": v(45.12, 9.3) * mm, "end": v(45.25, 9.4) * mm});
            skArc(sketch, "E276", {"start": v(45.25, 9.4) * mm, "mid": v(45.41, 9.47) * mm, "end": v(45.58, 9.53) * mm});
            skArc(sketch, "E277", {"start": v(45.58, 9.53) * mm, "mid": v(45.74, 9.57) * mm, "end": v(45.91, 9.58) * mm});
            skArc(sketch, "E278", {"start": v(45.91, 9.58) * mm, "mid": v(46.13, 9.56) * mm, "end": v(46.34, 9.5) * mm});
            skArc(sketch, "E279", {"start": v(46.34, 9.5) * mm, "mid": v(46.48, 9.42) * mm, "end": v(46.58, 9.3) * mm});
            skArc(sketch, "E280", {"start": v(46.58, 9.3) * mm, "mid": v(46.65, 9.08) * mm, "end": v(46.68, 8.87) * mm});
            skArc(sketch, "E281", {"start": v(46.68, 8.87) * mm, "mid": v(46.67, 8.44) * mm, "end": v(46.66, 8.01) * mm});
            skArc(sketch, "E282", {"start": v(46.66, 8.01) * mm, "mid": v(46.63, 7.7) * mm, "end": v(46.6, 7.4) * mm});
            skArc(sketch, "E283", {"start": v(46.6, 7.4) * mm, "mid": v(46.56, 7.12) * mm, "end": v(46.52, 6.85) * mm});
            skArc(sketch, "E284", {"start": v(46.52, 6.85) * mm, "mid": v(46.47, 6.63) * mm, "end": v(46.41, 6.4) * mm});
            skArc(sketch, "E285", {"start": v(46.41, 6.4) * mm, "mid": v(46.37, 6.32) * mm, "end": v(46.3, 6.24) * mm});
            skArc(sketch, "E286", {"start": v(46.3, 6.24) * mm, "mid": v(46.12, 6.03) * mm, "end": v(46, 5.77) * mm});
            skArc(sketch, "E287", {"start": v(46, 5.77) * mm, "mid": v(45.6, 4) * mm, "end": v(45.2, 2.25) * mm});
            skArc(sketch, "E288", {"start": v(45.2, 2.25) * mm, "mid": v(44.82, 0.56) * mm, "end": v(44.47, -1.14) * mm});
            skArc(sketch, "E289", {"start": v(44.47, -1.14) * mm, "mid": v(44.25, -2.34) * mm, "end": v(44.08, -3.56) * mm});
            skArc(sketch, "E290", {"start": v(44.08, -3.56) * mm, "mid": v(43.96, -5.36) * mm, "end": v(44.05, -7.17) * mm});
            skArc(sketch, "E291", {"start": v(44.05, -7.17) * mm, "mid": v(44.35, -9.14) * mm, "end": v(44.82, -11.07) * mm});
            skArc(sketch, "E292", {"start": v(44.82, -11.07) * mm, "mid": v(45.43, -12.87) * mm, "end": v(46.2, -14.6) * mm});
            skArc(sketch, "E293", {"start": v(46.2, -14.6) * mm, "mid": v(46.99, -15.92) * mm, "end": v(47.99, -17.08) * mm});
            skArc(sketch, "E294", {"start": v(47.99, -17.08) * mm, "mid": v(48.28, -17.34) * mm, "end": v(48.6, -17.6) * mm});
            skArc(sketch, "E295", {"start": v(48.6, -17.6) * mm, "mid": v(48.98, -17.85) * mm, "end": v(49.37, -18.1) * mm});
            skArc(sketch, "E296", {"start": v(49.37, -18.1) * mm, "mid": v(49.77, -18.33) * mm, "end": v(50.18, -18.54) * mm});
            skArc(sketch, "E297", {"start": v(50.18, -18.54) * mm, "mid": v(50.53, -18.69) * mm, "end": v(50.9, -18.81) * mm});
            skArc(sketch, "E298", {"start": v(50.9, -18.81) * mm, "mid": v(51.57, -18.97) * mm, "end": v(52.25, -19.05) * mm});
            skArc(sketch, "E299", {"start": v(52.25, -19.05) * mm, "mid": v(53.04, -19.07) * mm, "end": v(53.83, -19.03) * mm});
            skArc(sketch, "E300", {"start": v(53.83, -19.03) * mm, "mid": v(54.52, -18.94) * mm, "end": v(55.2, -18.81) * mm});
            skArc(sketch, "E301", {"start": v(55.2, -18.81) * mm, "mid": v(55.44, -18.66) * mm, "end": v(55.53, -18.4) * mm});
            skArc(sketch, "E302", {"start": v(55.53, -18.4) * mm, "mid": v(55.55, -18.31) * mm, "end": v(55.6, -18.24) * mm});
            skArc(sketch, "E303", {"start": v(55.6, -18.24) * mm, "mid": v(55.73, -18.16) * mm, "end": v(55.87, -18.08) * mm});
            skArc(sketch, "E304", {"start": v(55.87, -18.08) * mm, "mid": v(56.05, -18) * mm, "end": v(56.24, -17.93) * mm});
            skArc(sketch, "E305", {"start": v(56.24, -17.93) * mm, "mid": v(56.46, -17.86) * mm, "end": v(56.68, -17.8) * mm});
            skArc(sketch, "E306", {"start": v(56.68, -17.8) * mm, "mid": v(57.3, -17.6) * mm, "end": v(57.83, -17.24) * mm});
            skArc(sketch, "E307", {"start": v(57.83, -17.24) * mm, "mid": v(59.27, -16.01) * mm, "end": v(60.68, -14.76) * mm});
            skArc(sketch, "E308", {"start": v(60.68, -14.76) * mm, "mid": v(62.1, -13.46) * mm, "end": v(63.52, -12.14) * mm});
            skArc(sketch, "E309", {"start": v(63.52, -12.14) * mm, "mid": v(63.78, -11.77) * mm, "end": v(63.87, -11.32) * mm});
            skArc(sketch, "E310", {"start": v(63.87, -11.32) * mm, "mid": v(63.88, -11.22) * mm, "end": v(63.92, -11.13) * mm});
            skArc(sketch, "E311", {"start": v(63.92, -11.13) * mm, "mid": v(64.05, -10.93) * mm, "end": v(64.18, -10.73) * mm});
            skArc(sketch, "E312", {"start": v(64.18, -10.73) * mm, "mid": v(64.35, -10.5) * mm, "end": v(64.52, -10.26) * mm});
            skArc(sketch, "E313", {"start": v(64.52, -10.26) * mm, "mid": v(64.72, -10.01) * mm, "end": v(64.93, -9.77) * mm});
            skArc(sketch, "E314", {"start": v(64.93, -9.77) * mm, "mid": v(65.18, -9.47) * mm, "end": v(65.4, -9.14) * mm});
            skArc(sketch, "E315", {"start": v(65.4, -9.14) * mm, "mid": v(65.7, -8.68) * mm, "end": v(66, -8.21) * mm});
            skArc(sketch, "E316", {"start": v(66, -8.21) * mm, "mid": v(66.29, -7.7) * mm, "end": v(66.57, -7.17) * mm});
            skArc(sketch, "E317", {"start": v(66.57, -7.17) * mm, "mid": v(66.83, -6.67) * mm, "end": v(67.07, -6.16) * mm});
            skArc(sketch, "E318", {"start": v(67.07, -6.16) * mm, "mid": v(67.28, -5.7) * mm, "end": v(67.51, -5.24) * mm});
            skArc(sketch, "E319", {"start": v(67.51, -5.24) * mm, "mid": v(67.72, -4.85) * mm, "end": v(67.95, -4.47) * mm});
            skArc(sketch, "E320", {"start": v(67.95, -4.47) * mm, "mid": v(68.14, -4.17) * mm, "end": v(68.34, -3.87) * mm});
            skArc(sketch, "E321", {"start": v(68.34, -3.87) * mm, "mid": v(68.43, -3.8) * mm, "end": v(68.54, -3.77) * mm});
            skArc(sketch, "E322", {"start": v(68.54, -3.77) * mm, "mid": v(68.6, -3.76) * mm, "end": v(68.67, -3.74) * mm});
            skArc(sketch, "E323", {"start": v(68.67, -3.74) * mm, "mid": v(68.71, -3.7) * mm, "end": v(68.74, -3.65) * mm});
            skArc(sketch, "E324", {"start": v(68.74, -3.65) * mm, "mid": v(68.75, -3.6) * mm, "end": v(68.75, -3.53) * mm});
            skArc(sketch, "E325", {"start": v(68.75, -3.53) * mm, "mid": v(68.72, -3.45) * mm, "end": v(68.69, -3.38) * mm});
            skArc(sketch, "E326", {"start": v(68.69, -3.38) * mm, "mid": v(68.65, -3.3) * mm, "end": v(68.62, -3.23) * mm});
            skArc(sketch, "E327", {"start": v(68.62, -3.23) * mm, "mid": v(68.61, -3.15) * mm, "end": v(68.62, -3.07) * mm});
            skArc(sketch, "E328", {"start": v(68.62, -3.07) * mm, "mid": v(68.64, -3) * mm, "end": v(68.67, -2.95) * mm});
            skArc(sketch, "E329", {"start": v(68.67, -2.95) * mm, "mid": v(68.72, -2.9) * mm, "end": v(68.78, -2.86) * mm});
            skArc(sketch, "E330", {"start": v(68.78, -2.86) * mm, "mid": v(69.13, -2.65) * mm, "end": v(69.4, -2.33) * mm});
            skArc(sketch, "E331", {"start": v(69.4, -2.33) * mm, "mid": v(70.2, -1) * mm, "end": v(70.99, 0.35) * mm});
            skArc(sketch, "E332", {"start": v(70.99, 0.35) * mm, "mid": v(71.76, 1.73) * mm, "end": v(72.51, 3.13) * mm});
            skArc(sketch, "E333", {"start": v(72.51, 3.13) * mm, "mid": v(73.06, 4.26) * mm, "end": v(73.56, 5.4) * mm});
            skArc(sketch, "E334", {"start": v(73.56, 5.4) * mm, "mid": v(74.17, 6.96) * mm, "end": v(74.73, 8.52) * mm});
            skArc(sketch, "E335", {"start": v(74.73, 8.52) * mm, "mid": v(75.15, 9.83) * mm, "end": v(75.5, 11.15) * mm});
            skArc(sketch, "E336", {"start": v(75.5, 11.15) * mm, "mid": v(75.77, 12.43) * mm, "end": v(75.97, 13.73) * mm});
            skArc(sketch, "E337", {"start": v(75.97, 13.73) * mm, "mid": v(76.14, 15.21) * mm, "end": v(76.26, 16.7) * mm});
            skArc(sketch, "E338", {"start": v(76.26, 16.7) * mm, "mid": v(76.32, 18.21) * mm, "end": v(76.34, 19.73) * mm});
            skArc(sketch, "E339", {"start": v(76.34, 19.73) * mm, "mid": v(76.28, 20.57) * mm, "end": v(76.08, 21.39) * mm});
            skArc(sketch, "E340", {"start": v(76.08, 21.39) * mm, "mid": v(75.83, 21.85) * mm, "end": v(75.43, 22.2) * mm});
            skArc(sketch, "E341", {"start": v(75.43, 22.2) * mm, "mid": v(74.93, 22.4) * mm, "end": v(74.39, 22.43) * mm});
            skArc(sketch, "E342", {"start": v(74.39, 22.43) * mm, "mid": v(74.03, 22.33) * mm, "end": v(73.72, 22.14) * mm});
            skArc(sketch, "E343", {"start": v(73.72, 22.14) * mm, "mid": v(73.45, 21.86) * mm, "end": v(73.26, 21.52) * mm});
            skArc(sketch, "E344", {"start": v(73.26, 21.52) * mm, "mid": v(73.02, 20.88) * mm, "end": v(72.83, 20.21) * mm});
            skArc(sketch, "E345", {"start": v(72.83, 20.21) * mm, "mid": v(72.4, 18.44) * mm, "end": v(72, 16.67) * mm});
            skArc(sketch, "E346", {"start": v(72, 16.67) * mm, "mid": v(71.02, 12.75) * mm, "end": v(69.9, 8.88) * mm});
            skArc(sketch, "E347", {"start": v(69.9, 8.88) * mm, "mid": v(68.83, 5.74) * mm, "end": v(67.56, 2.68) * mm});
            skArc(sketch, "E348", {"start": v(67.56, 2.68) * mm, "mid": v(66.2, -0.07) * mm, "end": v(64.64, -2.72) * mm});
            skArc(sketch, "E349", {"start": v(64.64, -2.72) * mm, "mid": v(62.8, -5.44) * mm, "end": v(60.8, -8.06) * mm});
            skArc(sketch, "E350", {"start": v(60.8, -8.06) * mm, "mid": v(60.19, -8.77) * mm, "end": v(59.53, -9.44) * mm});
            skArc(sketch, "E351", {"start": v(59.53, -9.44) * mm, "mid": v(58.9, -10) * mm, "end": v(58.23, -10.5) * mm});
            skArc(sketch, "E352", {"start": v(58.23, -10.5) * mm, "mid": v(57.7, -10.81) * mm, "end": v(57.13, -11.08) * mm});
            skArc(sketch, "E353", {"start": v(57.13, -11.08) * mm, "mid": v(56.84, -11.09) * mm, "end": v(56.6, -10.9) * mm});
            skArc(sketch, "E354", {"start": v(56.6, -10.9) * mm, "mid": v(56.55, -10.78) * mm, "end": v(56.53, -10.65) * mm});
            skArc(sketch, "E355", {"start": v(56.53, -10.65) * mm, "mid": v(56.54, -10.32) * mm, "end": v(56.55, -9.98) * mm});
            skArc(sketch, "E356", {"start": v(56.55, -9.98) * mm, "mid": v(56.59, -9.58) * mm, "end": v(56.63, -9.18) * mm});
            skArc(sketch, "E357", {"start": v(56.63, -9.18) * mm, "mid": v(56.7, -8.74) * mm, "end": v(56.76, -8.3) * mm});
            skArc(sketch, "E358", {"start": v(56.76, -8.3) * mm, "mid": v(56.85, -7.73) * mm, "end": v(56.93, -7.16) * mm});
            skArc(sketch, "E359", {"start": v(56.93, -7.16) * mm, "mid": v(57.02, -6.32) * mm, "end": v(57.1, -5.5) * mm});
            skArc(sketch, "E360", {"start": v(57.1, -5.5) * mm, "mid": v(57.2, -4.57) * mm, "end": v(57.28, -3.65) * mm});
            skArc(sketch, "E361", {"start": v(57.28, -3.65) * mm, "mid": v(57.34, -2.77) * mm, "end": v(57.4, -1.89) * mm});
            skArc(sketch, "E362", {"start": v(57.4, -1.89) * mm, "mid": v(57.46, -0.95) * mm, "end": v(57.53, -0.02) * mm});
            skArc(sketch, "E363", {"start": v(57.53, -0.02) * mm, "mid": v(57.62, 1.07) * mm, "end": v(57.71, 2.15) * mm});
            skArc(sketch, "E364", {"start": v(57.71, 2.15) * mm, "mid": v(57.8, 3.22) * mm, "end": v(57.9, 4.29) * mm});
            skArc(sketch, "E365", {"start": v(57.9, 4.29) * mm, "mid": v(58, 5.15) * mm, "end": v(58.1, 6.02) * mm});
            skArc(sketch, "E366", {"start": v(58.1, 6.02) * mm, "mid": v(58.27, 7.97) * mm, "end": v(58.36, 9.93) * mm});
            skArc(sketch, "E367", {"start": v(58.36, 9.93) * mm, "mid": v(58.3, 11.36) * mm, "end": v(58.05, 12.77) * mm});
            skArc(sketch, "E368", {"start": v(58.05, 12.77) * mm, "mid": v(57.67, 13.95) * mm, "end": v(57.1, 15.05) * mm});
            skArc(sketch, "E369", {"start": v(57.1, 15.05) * mm, "mid": v(56.33, 16.17) * mm, "end": v(55.43, 17.18) * mm});
            skArc(sketch, "E370", {"start": v(55.43, 17.18) * mm, "mid": v(55.3, 17.32) * mm, "end": v(55.15, 17.44) * mm});
            skArc(sketch, "E371", {"start": v(55.15, 17.44) * mm, "mid": v(55.03, 17.53) * mm, "end": v(54.91, 17.61) * mm});
            skArc(sketch, "E372", {"start": v(54.91, 17.61) * mm, "mid": v(54.83, 17.64) * mm, "end": v(54.75, 17.66) * mm});
            skArc(sketch, "E373", {"start": v(54.75, 17.66) * mm, "mid": v(54.7, 17.65) * mm, "end": v(54.69, 17.6) * mm});
            skArc(sketch, "E374", {"start": v(54.69, 17.6) * mm, "mid": v(54.68, 17.56) * mm, "end": v(54.66, 17.53) * mm});
            skArc(sketch, "E375", {"start": v(54.66, 17.53) * mm, "mid": v(54.63, 17.5) * mm, "end": v(54.6, 17.5) * mm});
            skArc(sketch, "E376", {"start": v(54.6, 17.5) * mm, "mid": v(54.54, 17.53) * mm, "end": v(54.5, 17.57) * mm});
            skArc(sketch, "E377", {"start": v(54.5, 17.57) * mm, "mid": v(54.43, 17.64) * mm, "end": v(54.38, 17.71) * mm});
            skArc(sketch, "E378", {"start": v(54.38, 17.71) * mm, "mid": v(54.03, 18.1) * mm, "end": v(53.62, 18.4) * mm});
            skArc(sketch, "E379", {"start": v(53.62, 18.4) * mm, "mid": v(53, 18.73) * mm, "end": v(52.35, 19) * mm});
            skArc(sketch, "E380", {"start": v(52.35, 19) * mm, "mid": v(51.64, 19.26) * mm, "end": v(50.9, 19.44) * mm});
            skArc(sketch, "E381", {"start": v(50.9, 19.44) * mm, "mid": v(50.22, 19.55) * mm, "end": v(49.52, 19.59) * mm});
            skArc(sketch, "E382", {"start": v(49.52, 19.59) * mm, "mid": v(48.98, 19.57) * mm, "end": v(48.44, 19.52) * mm});
            skArc(sketch, "E383", {"start": v(48.44, 19.52) * mm, "mid": v(48.03, 19.44) * mm, "end": v(47.64, 19.3) * mm});
            skArc(sketch, "E384", {"start": v(47.64, 19.3) * mm, "mid": v(47.24, 19.1) * mm, "end": v(46.87, 18.86) * mm});
            skArc(sketch, "E385", {"start": v(46.87, 18.86) * mm, "mid": v(46.35, 18.45) * mm, "end": v(45.85, 18.02) * mm});
            skArc(sketch, "E386", {"start": v(45.85, 18.02) * mm, "mid": v(44.56, 16.8) * mm, "end": v(43.34, 15.5) * mm});
            skArc(sketch, "E387", {"start": v(43.34, 15.5) * mm, "mid": v(41.91, 13.8) * mm, "end": v(40.54, 12.06) * mm});
            skArc(sketch, "E388", {"start": v(40.54, 12.06) * mm, "mid": v(39.06, 10.06) * mm, "end": v(37.65, 8.02) * mm});
            skArc(sketch, "E389", {"start": v(37.65, 8.02) * mm, "mid": v(36.23, 5.83) * mm, "end": v(34.86, 3.61) * mm});
            skArc(sketch, "E390", {"start": v(34.86, 3.61) * mm, "mid": v(34.5, 2.99) * mm, "end": v(34.11, 2.37) * mm});
            skArc(sketch, "E391", {"start": v(34.11, 2.37) * mm, "mid": v(33.79, 1.86) * mm, "end": v(33.46, 1.35) * mm});
            skArc(sketch, "E392", {"start": v(33.46, 1.35) * mm, "mid": v(33.17, 0.92) * mm, "end": v(32.89, 0.5) * mm});
            skArc(sketch, "E393", {"start": v(32.89, 0.5) * mm, "mid": v(32.84, 0.47) * mm, "end": v(32.8, 0.48) * mm});
            skArc(sketch, "E394", {"start": v(32.8, 0.48) * mm, "mid": v(32.76, 0.54) * mm, "end": v(32.74, 0.6) * mm});
            skArc(sketch, "E395", {"start": v(32.74, 0.6) * mm, "mid": v(32.68, 1.1) * mm, "end": v(32.62, 1.6) * mm});
            skArc(sketch, "E396", {"start": v(32.62, 1.6) * mm, "mid": v(32.56, 2.18) * mm, "end": v(32.5, 2.75) * mm});
            skArc(sketch, "E397", {"start": v(32.5, 2.75) * mm, "mid": v(32.44, 3.43) * mm, "end": v(32.39, 4.1) * mm});
            skArc(sketch, "E398", {"start": v(32.39, 4.1) * mm, "mid": v(32.26, 5.34) * mm, "end": v(32.1, 6.58) * mm});
            skArc(sketch, "E399", {"start": v(32.1, 6.58) * mm, "mid": v(31.94, 7.46) * mm, "end": v(31.7, 8.33) * mm});
            skArc(sketch, "E400", {"start": v(31.7, 8.33) * mm, "mid": v(31.48, 8.9) * mm, "end": v(31.18, 9.46) * mm});
            skArc(sketch, "E401", {"start": v(31.18, 9.46) * mm, "mid": v(30.9, 9.75) * mm, "end": v(30.53, 9.92) * mm});
            skArc(sketch, "E402", {"start": v(30.53, 9.92) * mm, "mid": v(30.01, 9.95) * mm, "end": v(29.5, 9.8) * mm});
            skArc(sketch, "E403", {"start": v(29.5, 9.8) * mm, "mid": v(28.72, 9.42) * mm, "end": v(27.96, 8.97) * mm});
            skArc(sketch, "E404", {"start": v(27.96, 8.97) * mm, "mid": v(27, 8.3) * mm, "end": v(26.1, 7.58) * mm});
            skArc(sketch, "E405", {"start": v(26.1, 7.58) * mm, "mid": v(25, 6.63) * mm, "end": v(23.95, 5.65) * mm});
            skArc(sketch, "E406", {"start": v(23.95, 5.65) * mm, "mid": v(23.37, 5.1) * mm, "end": v(22.78, 4.55) * mm});
            skArc(sketch, "E407", {"start": v(22.78, 4.55) * mm, "mid": v(22.27, 4.1) * mm, "end": v(21.75, 3.68) * mm});
            skArc(sketch, "E408", {"start": v(21.75, 3.68) * mm, "mid": v(21.31, 3.34) * mm, "end": v(20.88, 3) * mm});
            skArc(sketch, "E409", {"start": v(20.88, 3) * mm, "mid": v(20.77, 2.97) * mm, "end": v(20.66, 3.02) * mm});
            skArc(sketch, "E410", {"start": v(20.66, 3.02) * mm, "mid": v(20.52, 3.27) * mm, "end": v(20.5, 3.55) * mm});
            skArc(sketch, "E411", {"start": v(20.5, 3.55) * mm, "mid": v(20.7, 4.37) * mm, "end": v(20.92, 5.2) * mm});
            skArc(sketch, "E412", {"start": v(20.92, 5.2) * mm, "mid": v(21.17, 6) * mm, "end": v(21.44, 6.8) * mm});
            skArc(sketch, "E413", {"start": v(21.44, 6.8) * mm, "mid": v(21.6, 7) * mm, "end": v(21.83, 7.08) * mm});
            skArc(sketch, "E414", {"start": v(21.83, 7.08) * mm, "mid": v(21.9, 7.08) * mm, "end": v(21.96, 7.1) * mm});
            skArc(sketch, "E415", {"start": v(21.96, 7.1) * mm, "mid": v(22, 7.14) * mm, "end": v(22.04, 7.19) * mm});
            skArc(sketch, "E416", {"start": v(22.04, 7.19) * mm, "mid": v(22.05, 7.25) * mm, "end": v(22.05, 7.3) * mm});
            skArc(sketch, "E417", {"start": v(22.05, 7.3) * mm, "mid": v(22.02, 7.38) * mm, "end": v(21.99, 7.45) * mm});
            skArc(sketch, "E418", {"start": v(21.99, 7.45) * mm, "mid": v(21.94, 7.57) * mm, "end": v(21.93, 7.7) * mm});
            skArc(sketch, "E419", {"start": v(21.93, 7.7) * mm, "mid": v(21.97, 7.97) * mm, "end": v(22.02, 8.25) * mm});
            skArc(sketch, "E420", {"start": v(22.02, 8.25) * mm, "mid": v(22.1, 8.58) * mm, "end": v(22.18, 8.92) * mm});
            skArc(sketch, "E421", {"start": v(22.18, 8.92) * mm, "mid": v(22.3, 9.28) * mm, "end": v(22.42, 9.64) * mm});
            skArc(sketch, "E422", {"start": v(22.42, 9.64) * mm, "mid": v(22.55, 10) * mm, "end": v(22.68, 10.38) * mm});
            skArc(sketch, "E423", {"start": v(22.68, 10.38) * mm, "mid": v(22.8, 10.74) * mm, "end": v(22.92, 11.1) * mm});
            skArc(sketch, "E424", {"start": v(22.92, 11.1) * mm, "mid": v(23.02, 11.42) * mm, "end": v(23.12, 11.73) * mm});
            skArc(sketch, "E425", {"start": v(23.12, 11.73) * mm, "mid": v(23.17, 11.9) * mm, "end": v(23.22, 12.08) * mm});
            skArc(sketch, "E426", {"start": v(23.22, 12.08) * mm, "mid": v(23.24, 12.2) * mm, "end": v(23.27, 12.32) * mm});
            skArc(sketch, "E427", {"start": v(23.27, 12.32) * mm, "mid": v(23.3, 12.42) * mm, "end": v(23.33, 12.52) * mm});
            skArc(sketch, "E428", {"start": v(23.33, 12.52) * mm, "mid": v(23.36, 12.6) * mm, "end": v(23.4, 12.69) * mm});
            skArc(sketch, "E429", {"start": v(23.4, 12.69) * mm, "mid": v(23.4, 12.7) * mm, "end": v(23.42, 12.7) * mm});
            skArc(sketch, "E430", {"start": v(23.42, 12.7) * mm, "mid": v(23.64, 12.8) * mm, "end": v(23.74, 13) * mm});
            skArc(sketch, "E431", {"start": v(23.74, 13) * mm, "mid": v(23.83, 14.26) * mm, "end": v(23.9, 15.52) * mm});
            skArc(sketch, "E432", {"start": v(23.9, 15.52) * mm, "mid": v(23.94, 16.75) * mm, "end": v(23.96, 17.97) * mm});
            skArc(sketch, "E433", {"start": v(23.96, 17.97) * mm, "mid": v(23.9, 18.47) * mm, "end": v(23.72, 18.94) * mm});
            skArc(sketch, "E434", {"start": v(23.72, 18.94) * mm, "mid": v(23.19, 19.74) * mm, "end": v(22.48, 20.39) * mm});
            skArc(sketch, "E435", {"start": v(22.48, 20.39) * mm, "mid": v(21.4, 21.1) * mm, "end": v(20.25, 21.71) * mm});
            skArc(sketch, "E436", {"start": v(20.25, 21.71) * mm, "mid": v(19, 22.23) * mm, "end": v(17.7, 22.63) * mm});
            skArc(sketch, "E437", {"start": v(17.7, 22.63) * mm, "mid": v(16.56, 22.83) * mm, "end": v(15.42, 22.85) * mm});
            skArc(sketch, "E438", {"start": v(15.42, 22.85) * mm, "mid": v(14.95, 22.81) * mm, "end": v(14.48, 22.74) * mm});
            skArc(sketch, "E439", {"start": v(14.48, 22.74) * mm, "mid": v(14.2, 22.66) * mm, "end": v(13.94, 22.52) * mm});
            skArc(sketch, "E440", {"start": v(13.94, 22.52) * mm, "mid": v(13.72, 22.33) * mm, "end": v(13.55, 22.1) * mm});
            skArc(sketch, "E441", {"start": v(13.55, 22.1) * mm, "mid": v(13.33, 21.7) * mm, "end": v(13.14, 21.28) * mm});
            skArc(sketch, "E442", {"start": v(13.14, 21.28) * mm, "mid": v(12.96, 20.83) * mm, "end": v(12.82, 20.36) * mm});
            skArc(sketch, "E443", {"start": v(12.82, 20.36) * mm, "mid": v(12.58, 19.39) * mm, "end": v(12.34, 18.4) * mm});
            skArc(sketch, "E444", {"start": v(12.34, 18.4) * mm, "mid": v(12.08, 17.24) * mm, "end": v(11.82, 16.08) * mm});
            skArc(sketch, "E445", {"start": v(11.82, 16.08) * mm, "mid": v(11.57, 14.84) * mm, "end": v(11.33, 13.6) * mm});
            skArc(sketch, "E446", {"start": v(11.33, 13.6) * mm, "mid": v(11.09, 12.38) * mm, "end": v(10.83, 11.17) * mm});
            skArc(sketch, "E447", {"start": v(10.83, 11.17) * mm, "mid": v(10.6, 10.1) * mm, "end": v(10.33, 9.04) * mm});
            skArc(sketch, "E448", {"start": v(10.33, 9.04) * mm, "mid": v(10.1, 8.16) * mm, "end": v(9.85, 7.28) * mm});
            skArc(sketch, "E449", {"start": v(9.85, 7.28) * mm, "mid": v(9.75, 7.03) * mm, "end": v(9.58, 6.82) * mm});
            skArc(sketch, "E450", {"start": v(9.58, 6.82) * mm, "mid": v(9.42, 6.69) * mm, "end": v(9.23, 6.58) * mm});
            skArc(sketch, "E451", {"start": v(9.23, 6.58) * mm, "mid": v(8.92, 6.45) * mm, "end": v(8.6, 6.34) * mm});
            skArc(sketch, "E452", {"start": v(8.6, 6.34) * mm, "mid": v(8.21, 6.22) * mm, "end": v(7.82, 6.13) * mm});
            skArc(sketch, "E453", {"start": v(7.82, 6.13) * mm, "mid": v(7.42, 6.04) * mm, "end": v(7.02, 5.98) * mm});
            skLineSegment(sketch, "E454", {"start": v(7.02, 5.98) * mm, "end": v(5.02, 5.7) * mm});
            skLineSegment(sketch, "E455", {"start": v(5.02, 5.7) * mm, "end": v(5.11, 10.87) * mm});
            skArc(sketch, "E456", {"start": v(5.11, 10.87) * mm, "mid": v(5.13, 12.63) * mm, "end": v(5.12, 14.38) * mm});
            skArc(sketch, "E457", {"start": v(5.12, 14.38) * mm, "mid": v(5.07, 15.59) * mm, "end": v(4.96, 16.8) * mm});
            skArc(sketch, "E458", {"start": v(4.96, 16.8) * mm, "mid": v(4.84, 17.59) * mm, "end": v(4.67, 18.38) * mm});
            skArc(sketch, "E459", {"start": v(4.67, 18.38) * mm, "mid": v(4.49, 18.65) * mm, "end": v(4.18, 18.75) * mm});
            skArc(sketch, "E460", {"start": v(4.18, 18.75) * mm, "mid": v(4.11, 18.76) * mm, "end": v(4.04, 18.78) * mm});
            skArc(sketch, "E461", {"start": v(4.04, 18.78) * mm, "mid": v(4, 18.81) * mm, "end": v(3.96, 18.86) * mm});
            skArc(sketch, "E462", {"start": v(3.96, 18.86) * mm, "mid": v(3.94, 18.92) * mm, "end": v(3.94, 18.98) * mm});
            skArc(sketch, "E463", {"start": v(3.94, 18.98) * mm, "mid": v(3.97, 19.05) * mm, "end": v(4, 19.12) * mm});
            skArc(sketch, "E464", {"start": v(4, 19.12) * mm, "mid": v(4.08, 19.41) * mm, "end": v(3.97, 19.7) * mm});
            skArc(sketch, "E465", {"start": v(3.97, 19.7) * mm, "mid": v(3.51, 20.28) * mm, "end": v(3.02, 20.82) * mm});
            skArc(sketch, "E466", {"start": v(3.02, 20.82) * mm, "mid": v(2.44, 21.38) * mm, "end": v(1.83, 21.9) * mm});
            skArc(sketch, "E467", {"start": v(1.83, 21.9) * mm, "mid": v(1.33, 22.23) * mm, "end": v(0.77, 22.49) * mm});
            skArc(sketch, "E468", {"start": v(0.77, 22.49) * mm, "mid": v(0.02, 22.71) * mm, "end": v(-0.75, 22.84) * mm});
            skArc(sketch, "E469", {"start": v(-0.75, 22.84) * mm, "mid": v(-1.6, 22.9) * mm, "end": v(-2.45, 22.87) * mm});
            skArc(sketch, "E470", {"start": v(-2.45, 22.87) * mm, "mid": v(-3.32, 22.75) * mm, "end": v(-4.18, 22.56) * mm});
            skArc(sketch, "E471", {"start": v(-4.18, 22.56) * mm, "mid": v(-5, 22.3) * mm, "end": v(-5.77, 21.94) * mm});
            skArc(sketch, "E472", {"start": v(-0.86, 18.64) * mm, "mid": v(-0.04, 17.52) * mm, "end": v(0.47, 16.22) * mm});
            skArc(sketch, "E473", {"start": v(0.47, 16.22) * mm, "mid": v(0.93, 14.13) * mm, "end": v(1.22, 12.02) * mm});
            skArc(sketch, "E474", {"start": v(1.22, 12.02) * mm, "mid": v(1.35, 10.04) * mm, "end": v(1.34, 8.06) * mm});
            skArc(sketch, "E475", {"start": v(1.34, 8.06) * mm, "mid": v(1.03, 7.36) * mm, "end": v(0.31, 7.08) * mm});
            skArc(sketch, "E476", {"start": v(0.31, 7.08) * mm, "mid": v(-0.04, 7.14) * mm, "end": v(-0.35, 7.33) * mm});
            skArc(sketch, "E477", {"start": v(-0.35, 7.33) * mm, "mid": v(-0.95, 7.89) * mm, "end": v(-1.52, 8.47) * mm});
            skArc(sketch, "E478", {"start": v(-1.52, 8.47) * mm, "mid": v(-2.07, 9.07) * mm, "end": v(-2.6, 9.69) * mm});
            skArc(sketch, "E479", {"start": v(-2.6, 9.69) * mm, "mid": v(-2.68, 9.91) * mm, "end": v(-2.58, 10.13) * mm});
            skArc(sketch, "E480", {"start": v(-2.58, 10.13) * mm, "mid": v(-2.54, 10.18) * mm, "end": v(-2.5, 10.24) * mm});
            skArc(sketch, "E481", {"start": v(-2.5, 10.24) * mm, "mid": v(-2.5, 10.28) * mm, "end": v(-2.5, 10.33) * mm});
            skArc(sketch, "E482", {"start": v(-2.5, 10.33) * mm, "mid": v(-2.54, 10.37) * mm, "end": v(-2.58, 10.4) * mm});
            skArc(sketch, "E483", {"start": v(-2.58, 10.4) * mm, "mid": v(-2.66, 10.4) * mm, "end": v(-2.73, 10.41) * mm});
            skArc(sketch, "E484", {"start": v(-2.73, 10.41) * mm, "mid": v(-3, 10.48) * mm, "end": v(-3.18, 10.67) * mm});
            skArc(sketch, "E485", {"start": v(-3.18, 10.67) * mm, "mid": v(-3.44, 11.16) * mm, "end": v(-3.67, 11.66) * mm});
            skArc(sketch, "E486", {"start": v(-3.67, 11.66) * mm, "mid": v(-3.88, 12.27) * mm, "end": v(-4.04, 12.9) * mm});
            skArc(sketch, "E487", {"start": v(-4.04, 12.9) * mm, "mid": v(-4.15, 13.5) * mm, "end": v(-4.2, 14.12) * mm});
            skArc(sketch, "E488", {"start": v(-4.2, 14.12) * mm, "mid": v(-4.2, 14.38) * mm, "end": v(-4.23, 14.65) * mm});
            skArc(sketch, "E489", {"start": v(-4.23, 14.65) * mm, "mid": v(-4.27, 14.89) * mm, "end": v(-4.33, 15.13) * mm});
            skArc(sketch, "E490", {"start": v(-4.33, 15.13) * mm, "mid": v(-4.39, 15.32) * mm, "end": v(-4.46, 15.5) * mm});
            skArc(sketch, "E491", {"start": v(-4.46, 15.5) * mm, "mid": v(-4.52, 15.6) * mm, "end": v(-4.6, 15.68) * mm});
            skArc(sketch, "E492", {"start": v(-4.6, 15.68) * mm, "mid": v(-4.77, 15.86) * mm, "end": v(-4.83, 16.1) * mm});
            skArc(sketch, "E493", {"start": v(-4.83, 16.1) * mm, "mid": v(-4.78, 16.64) * mm, "end": v(-4.7, 17.18) * mm});
            skArc(sketch, "E494", {"start": v(-4.7, 17.18) * mm, "mid": v(-4.58, 17.75) * mm, "end": v(-4.41, 18.31) * mm});
            skArc(sketch, "E495", {"start": v(-4.41, 18.31) * mm, "mid": v(-4.24, 18.7) * mm, "end": v(-4, 19.07) * mm});
            skArc(sketch, "E496", {"start": v(-4, 19.07) * mm, "mid": v(-3.73, 19.32) * mm, "end": v(-3.39, 19.48) * mm});
            skArc(sketch, "E497", {"start": v(-3.39, 19.48) * mm, "mid": v(-2.97, 19.56) * mm, "end": v(-2.55, 19.55) * mm});
            skArc(sketch, "E498", {"start": v(-2.55, 19.55) * mm, "mid": v(-2.08, 19.44) * mm, "end": v(-1.65, 19.25) * mm});
            skArc(sketch, "E499", {"start": v(-1.65, 19.25) * mm, "mid": v(-1.23, 18.98) * mm, "end": v(-0.86, 18.64) * mm});
            skArc(sketch, "E500", {"start": v(-2, 4.15) * mm, "mid": v(-1.68, 3.98) * mm, "end": v(-1.36, 3.8) * mm});
            skArc(sketch, "E501", {"start": v(-1.36, 3.8) * mm, "mid": v(-1.1, 3.66) * mm, "end": v(-0.83, 3.5) * mm});
            skArc(sketch, "E502", {"start": v(-0.83, 3.5) * mm, "mid": v(-0.62, 3.36) * mm, "end": v(-0.4, 3.22) * mm});
            skArc(sketch, "E503", {"start": v(-0.4, 3.22) * mm, "mid": v(-0.36, 3.17) * mm, "end": v(-0.35, 3.1) * mm});
            skArc(sketch, "E504", {"start": v(-0.35, 3.1) * mm, "mid": v(-0.36, 3.03) * mm, "end": v(-0.38, 2.96) * mm});
            skArc(sketch, "E505", {"start": v(-0.38, 2.96) * mm, "mid": v(-0.56, 2.55) * mm, "end": v(-0.74, 2.14) * mm});
            skArc(sketch, "E506", {"start": v(-0.74, 2.14) * mm, "mid": v(-0.95, 1.67) * mm, "end": v(-1.16, 1.2) * mm});
            skArc(sketch, "E507", {"start": v(-1.16, 1.2) * mm, "mid": v(-1.42, 0.65) * mm, "end": v(-1.67, 0.1) * mm});
            skArc(sketch, "E508", {"start": v(-1.67, 0.1) * mm, "mid": v(-2.32, -1.11) * mm, "end": v(-3.07, -2.27) * mm});
            skArc(sketch, "E509", {"start": v(-3.07, -2.27) * mm, "mid": v(-4.1, -3.62) * mm, "end": v(-5.19, -4.92) * mm});
            skArc(sketch, "E510", {"start": v(-5.19, -4.92) * mm, "mid": v(-6.26, -6.1) * mm, "end": v(-7.36, -7.23) * mm});
            skArc(sketch, "E511", {"start": v(-7.36, -7.23) * mm, "mid": v(-7.78, -7.43) * mm, "end": v(-8.23, -7.33) * mm});
            skArc(sketch, "E512", {"start": v(-8.23, -7.33) * mm, "mid": v(-8.63, -6.91) * mm, "end": v(-8.75, -6.35) * mm});
            skArc(sketch, "E513", {"start": v(-8.75, -6.35) * mm, "mid": v(-8.64, -4.34) * mm, "end": v(-8.48, -2.34) * mm});
            skArc(sketch, "E514", {"start": v(-8.48, -2.34) * mm, "mid": v(-8.23, -0.1) * mm, "end": v(-7.9, 2.13) * mm});
            skArc(sketch, "E515", {"start": v(-7.9, 2.13) * mm, "mid": v(-7.48, 4.27) * mm, "end": v(-6.97, 6.38) * mm});
            skLineSegment(sketch, "E516", {"start": v(-6.97, 6.38) * mm, "end": v(-6.55, 7.98) * mm});
            skLineSegment(sketch, "E517", {"start": v(-6.55, 7.98) * mm, "end": v(-5.1, 6.48) * mm});
            skArc(sketch, "E518", {"start": v(-5.1, 6.48) * mm, "mid": v(-4.76, 6.16) * mm, "end": v(-4.42, 5.85) * mm});
            skArc(sketch, "E519", {"start": v(-4.42, 5.85) * mm, "mid": v(-4, 5.5) * mm, "end": v(-3.58, 5.18) * mm});
            skArc(sketch, "E520", {"start": v(-3.58, 5.18) * mm, "mid": v(-3.16, 4.87) * mm, "end": v(-2.73, 4.57) * mm});
            skArc(sketch, "E521", {"start": v(-2.73, 4.57) * mm, "mid": v(-2.37, 4.35) * mm, "end": v(-2, 4.15) * mm});
            skSolve(sketch);
        }
        {
            var Q0;
            Q0=makeQuery(id+"F0.imprint","IMPRINT",FACE,{"disambiguationData":[TD([[makeQuery(id+"F0.imprint","IMPRINT",EDGE,{"derivedFrom":sQuery(id+"F0.wireOp",EDGE,"E0")}),1.0]])]});
            extrude(context, id + "F1", {"entities" : qUnion([Q0]), "depth" : 1.5 * mm, "offsetDistance" : 25 * mm});
        }
        {
            var Q0;
            Q0=qCreatedBy(makeId("Top.planeOp"),FACE);
            var sketch = newSketch(context, id + "F2", { "sketchPlane" : qUnion([Q0])});
            skLineSegment(sketch, "E522.bottom", {"start": v(-1.9, -116.92) * mm, "end": v(2.1, -116.92) * mm});
            skLineSegment(sketch, "E522.top", {"start": v(-1.9, -1.92) * mm, "end": v(2.1, -1.92) * mm});
            skLineSegment(sketch, "E522.left", {"start": v(-1.9, -116.92) * mm, "end": v(-1.9, -1.92) * mm});
            skLineSegment(sketch, "E522.right", {"start": v(2.1, -116.92) * mm, "end": v(2.1, -1.92) * mm});
            skLineSegment(sketch, "E523", {"start": v(-1.9, -116.92) * mm, "end": v(0, -124.56) * mm});
            skLineSegment(sketch, "E524", {"start": v(0, -124.56) * mm, "end": v(2.1, -116.92) * mm});
            skSolve(sketch);
        }
        {
            var Q0;
            Q0 = qSketchRegion(id + "F2", true);
            extrude(context, id + "F3", {"entities" : qUnion([Q0]), "operationType" : NewBodyOperationType.ADD, "depth" : 1.5 * mm, "offsetDistance" : 25 * mm});
        }
    });
